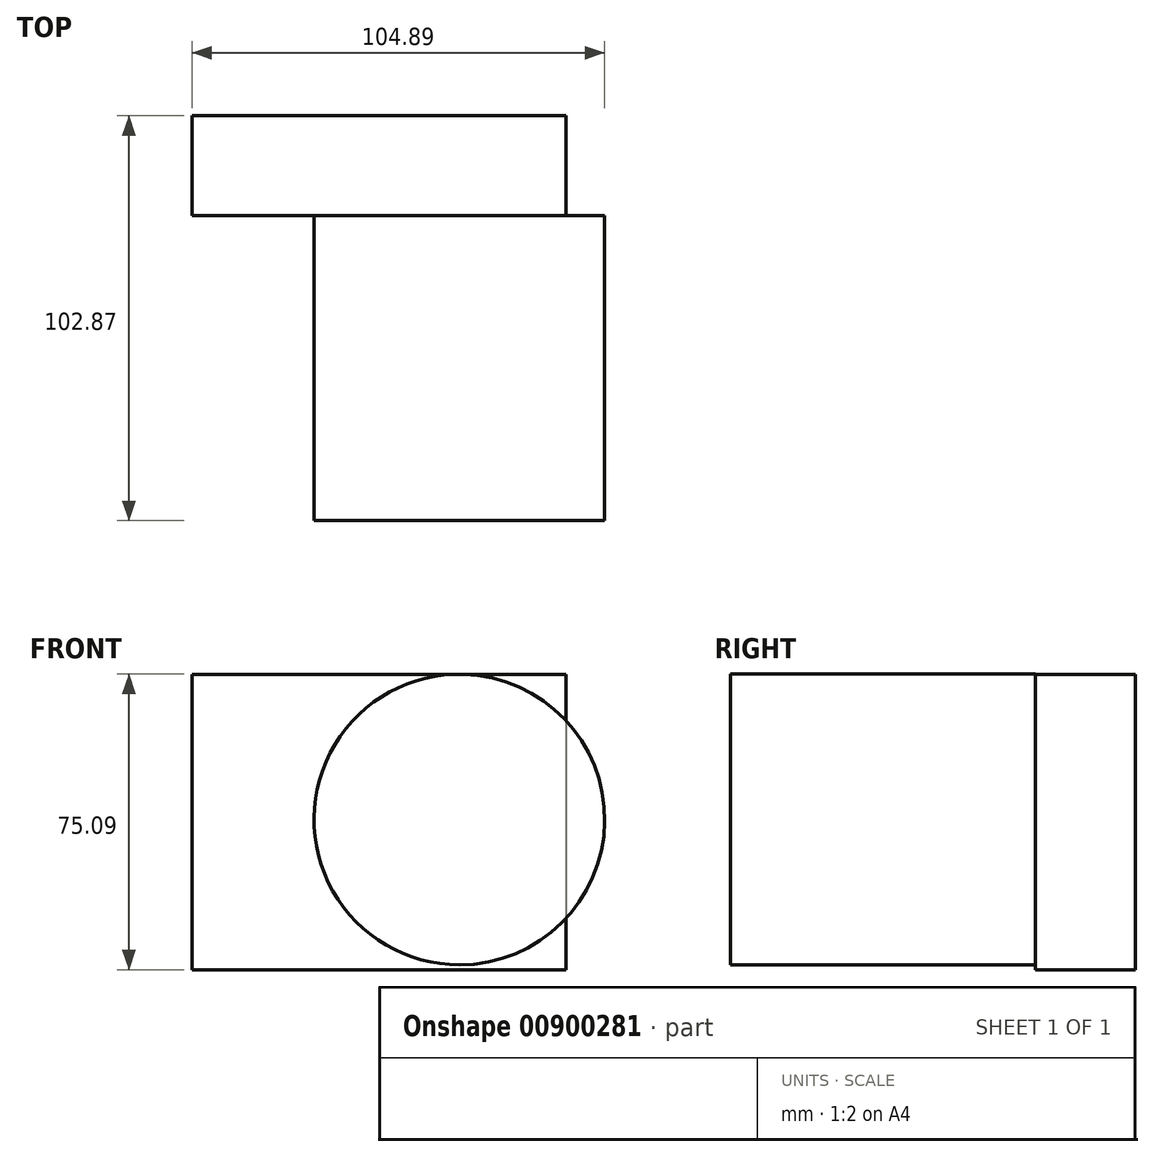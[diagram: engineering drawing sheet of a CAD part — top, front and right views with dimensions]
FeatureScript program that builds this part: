
annotation { "Feature Type Name" : "Feature", "Feature Type Description" : "" }
export const myFeature = defineFeature(function(context is Context, id is Id, definition is map)
    precondition{}
    {
        {
            var Q0;
            Q0=qCreatedBy(makeId("Front.planeOp"),FACE);
            var sketch = newSketch(context, id + "F0", { "sketchPlane" : qUnion([Q0])});
            skCircle(sketch, "E0", {"center": v(4.32, 0) * mm, "radius": 36.93 * mm});
            skSolve(sketch);
        }
        {
            var Q0;
            Q0=makeQuery(id+"F0.imprint","IMPRINT",FACE,{"disambiguationData":[TD([[makeQuery(id+"F0.imprint","IMPRINT",EDGE,{"derivedFrom":sQuery(id+"F0.wireOp",EDGE,"E0")}),1.0]])]});
            extrude(context, id + "F1", {"entities" : qUnion([Q0]), "depth" : 77.47 * mm, "offsetDistance" : 25.4 * mm});
        }
        {
            var Q0;
            Q0=qCreatedBy(makeId("Front.planeOp"),FACE);
            var sketch = newSketch(context, id + "F2", { "sketchPlane" : qUnion([Q0])});
            skLineSegment(sketch, "E1.bottom", {"start": v(-63.64, 36.92) * mm, "end": v(31.39, 36.92) * mm});
            skLineSegment(sketch, "E1.top", {"start": v(-63.64, -38.16) * mm, "end": v(31.39, -38.16) * mm});
            skLineSegment(sketch, "E1.left", {"start": v(-63.64, 36.92) * mm, "end": v(-63.64, -38.16) * mm});
            skLineSegment(sketch, "E1.right", {"start": v(31.39, 36.92) * mm, "end": v(31.39, -38.16) * mm});
            skSolve(sketch);
        }
        {
            var Q0;
            Q0=makeQuery(id+"F2.imprint","IMPRINT",FACE,{"disambiguationData":[TD([[makeQuery(id+"F2.imprint","IMPRINT",EDGE,{"derivedFrom":sQuery(id+"F2.wireOp",EDGE,"E1.bottom")}),-1.0]])]});
            extrude(context, id + "F3", {"entities" : qUnion([Q0]), "operationType" : NewBodyOperationType.ADD, "oppositeDirection" : true, "depth" : 25.4 * mm, "offsetDistance" : 25.4 * mm});
        }
    });
